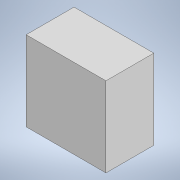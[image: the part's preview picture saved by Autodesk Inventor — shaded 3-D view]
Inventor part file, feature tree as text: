
AUTODESK INVENTOR PART (.ipt)
format: ipt  version: 2020 (Build 240168000, 168)  size: 85,504 bytes
history: native  units: mm
features: extrude x1, sketch x1
ambient origin geometry x8: Origin, YZ Plane, XZ Plane, XY Plane, X Axis, Y Axis, Z Axis, Center Point
bodies: Solid1 (feature_tree)
feature tree (2):
  extrude  "Extrusion1"  Depth=12.0mm
  sketch  "Sketch1"  dims[d0=20.0mm d1=12.0mm d2=20.0mm d3=0.0mm]
